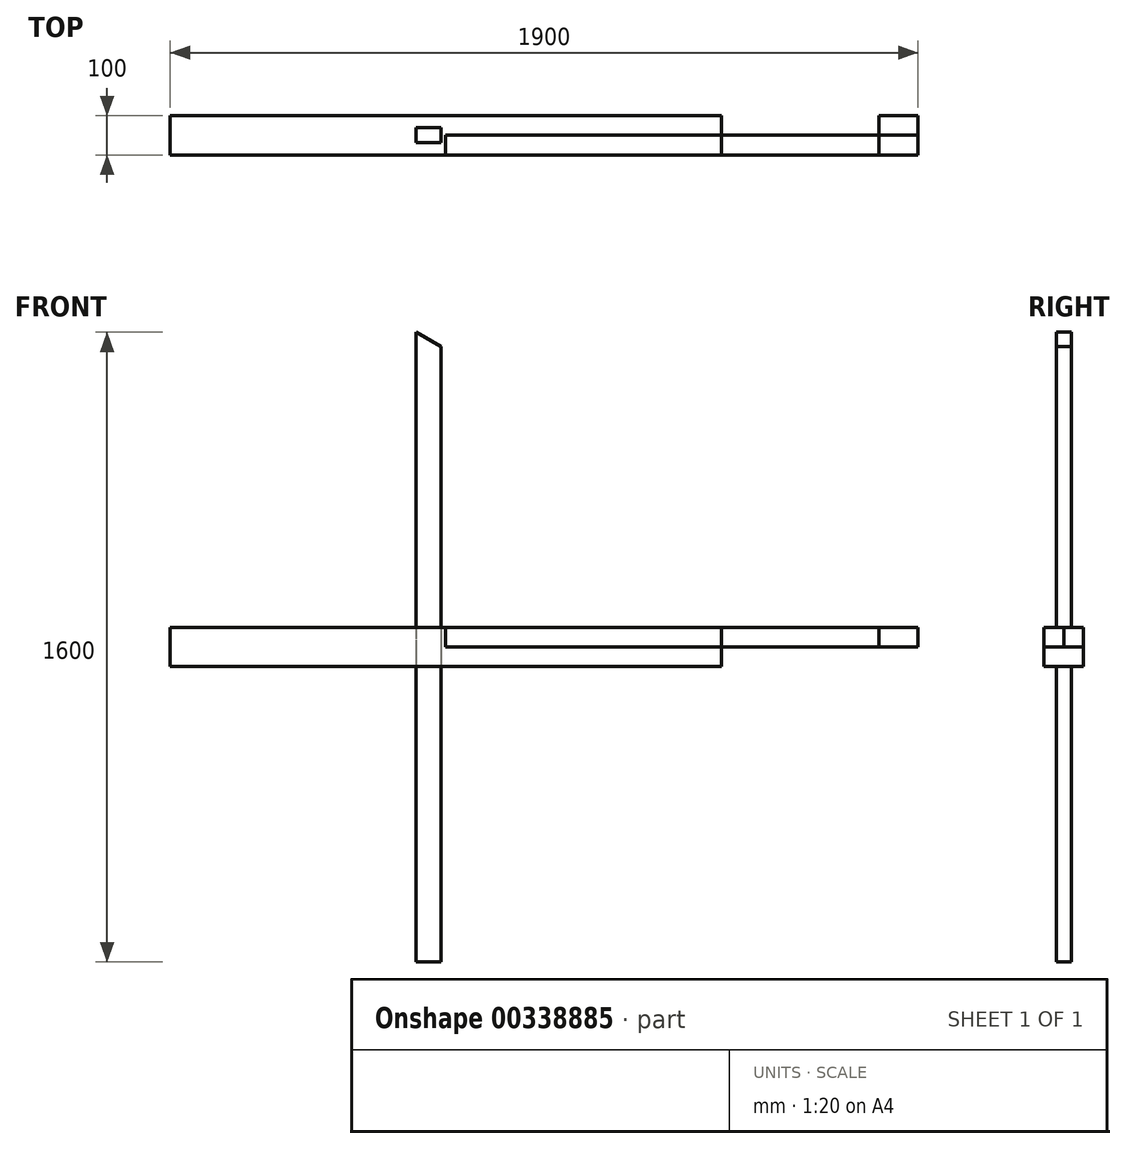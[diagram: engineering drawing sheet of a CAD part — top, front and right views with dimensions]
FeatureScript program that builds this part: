
annotation { "Feature Type Name" : "Feature", "Feature Type Description" : "" }
export const myFeature = defineFeature(function(context is Context, id is Id, definition is map)
    precondition{}
    {
        {
            var Q0;
            Q0=qCreatedBy(makeId("Front.planeOp"),FACE);
            var sketch = newSketch(context, id + "F0", { "sketchPlane" : qUnion([Q0])});
            skLineSegment(sketch, "E0.bottom", {"start": v(1200, 50) * mm, "end": v(-1200, 50) * mm});
            skLineSegment(sketch, "E0.top", {"start": v(1200, -50) * mm, "end": v(-1200, -50) * mm});
            skLineSegment(sketch, "E0.left", {"start": v(1200, 50) * mm, "end": v(1200, -50) * mm});
            skLineSegment(sketch, "E0.right", {"start": v(-1200, 50) * mm, "end": v(-1200, -50) * mm});
            skPoint(sketch, "E0.middle", {"position": v(0, 0) * mm});
            skPoint(sketch, "E1.middle", {"position": v(1200, 50) * mm});
            skLineSegment(sketch, "E2.bottom", {"start": v(1200, 50) * mm, "end": v(1100, 50) * mm});
            skLineSegment(sketch, "E2.top", {"start": v(1200, 0) * mm, "end": v(1100, 0) * mm});
            skLineSegment(sketch, "E2.left", {"start": v(1200, 50) * mm, "end": v(1200, 0) * mm});
            skLineSegment(sketch, "E2.right", {"start": v(1100, 50) * mm, "end": v(1100, 0) * mm});
            skSolve(sketch);
        }
        {
            var Q0;
            Q0=makeQuery(id+"F0.imprint","IMPRINT",FACE,{"disambiguationData":[TD([[makeQuery(id+"F0.imprint","IMPRINT",EDGE,{"derivedFrom":sQuery(id+"F0.wireOp",EDGE,"E0.bottom")}),1.0]])]});
            extrude(context, id + "F1", {"entities" : qUnion([Q0]), "endBound" : BoundingType.SYMMETRIC, "depth" : 100 * mm});
        }
        {
            var Q0;
            Q0=qCreatedBy(makeId("Front.planeOp"),FACE);
            var sketch = newSketch(context, id + "F2", { "sketchPlane" : qUnion([Q0])});
            skLineSegment(sketch, "E3.bottom", {"start": v(700, -50) * mm, "end": v(-700, -50) * mm});
            skLineSegment(sketch, "E3.top", {"start": v(700, 50) * mm, "end": v(-700, 50) * mm});
            skLineSegment(sketch, "E3.left", {"start": v(700, -50) * mm, "end": v(700, 50) * mm});
            skLineSegment(sketch, "E3.right", {"start": v(-700, -50) * mm, "end": v(-700, 50) * mm});
            skPoint(sketch, "E3.middle", {"position": v(0, 0) * mm});
            skSolve(sketch);
        }
        {
            var Q0;
            Q0=makeQuery(id+"F2.imprint","IMPRINT",FACE,{"disambiguationData":[TD([[makeQuery(id+"F2.imprint","IMPRINT",EDGE,{"derivedFrom":sQuery(id+"F2.wireOp",EDGE,"E3.bottom")}),-1.0]])]});
            extrude(context, id + "F3", {"entities" : qUnion([Q0]), "endBound" : BoundingType.SYMMETRIC, "depth" : 100 * mm});
        }
        {
            var Q0;
            Q0=qCreatedBy(makeId("Front.planeOp"),FACE);
            var sketch = newSketch(context, id + "F4", { "sketchPlane" : qUnion([Q0])});
            skLineSegment(sketch, "E4.bottom", {"start": v(-12.17, 800) * mm, "end": v(-75.17, 800) * mm});
            skLineSegment(sketch, "E4.top", {"start": v(-12.17, -800) * mm, "end": v(-75.17, -800) * mm});
            skLineSegment(sketch, "E4.left", {"start": v(-12.17, 800) * mm, "end": v(-12.17, -800) * mm});
            skLineSegment(sketch, "E4.right", {"start": v(-75.17, 800) * mm, "end": v(-75.17, -800) * mm});
            skPoint(sketch, "E4.middle", {"position": v(-43.67, 0) * mm});
            skSolve(sketch);
        }
        {
            var Q0;
            Q0 = qSketchRegion(id + "F4", true);
            extrude(context, id + "F5", {"entities" : qUnion([Q0]), "endBound" : BoundingType.SYMMETRIC, "depth" : 38 * mm});
        }
        {
            var Q0;
            Q0=makeQuery(id+"F5.opExtrude","SWEPT_EDGE",EDGE,{"disambiguationData":[OSD([sQuery(id+"F4.wireOp",EDGE,"E4.bottom"),sQuery(id+"F4.wireOp",EDGE,"E4.left")])]});
            chamfer(context, id + "F6", {"entities" : qUnion([Q0]), "chamferType" : ChamferType.OFFSET_ANGLE, "width" : 63 * mm, "oppositeDirection" : false, "angle" : 30 * degree, "tangentPropagation" : true});
        }
        {
            var Q0;
            Q0=qCreatedBy(makeId("Right.planeOp"),FACE);
            var sketch = newSketch(context, id + "F7", { "sketchPlane" : qUnion([Q0])});
            skLineSegment(sketch, "E5.bottom", {"start": v(-50, 50) * mm, "end": v(0, 50) * mm});
            skLineSegment(sketch, "E5.top", {"start": v(-50, 0) * mm, "end": v(0, 0) * mm});
            skLineSegment(sketch, "E5.left", {"start": v(-50, 50) * mm, "end": v(-50, 0) * mm});
            skLineSegment(sketch, "E5.right", {"start": v(0, 50) * mm, "end": v(0, 0) * mm});
            skPoint(sketch, "E5.middle", {"position": v(-25, 25) * mm});
            skSolve(sketch);
        }
        {
            var Q0;
            Q0 = qSketchRegion(id + "F7", true);
            extrude(context, id + "F8", {"entities" : qUnion([Q0]), "depth" : 1200 * mm});
        }
    });
